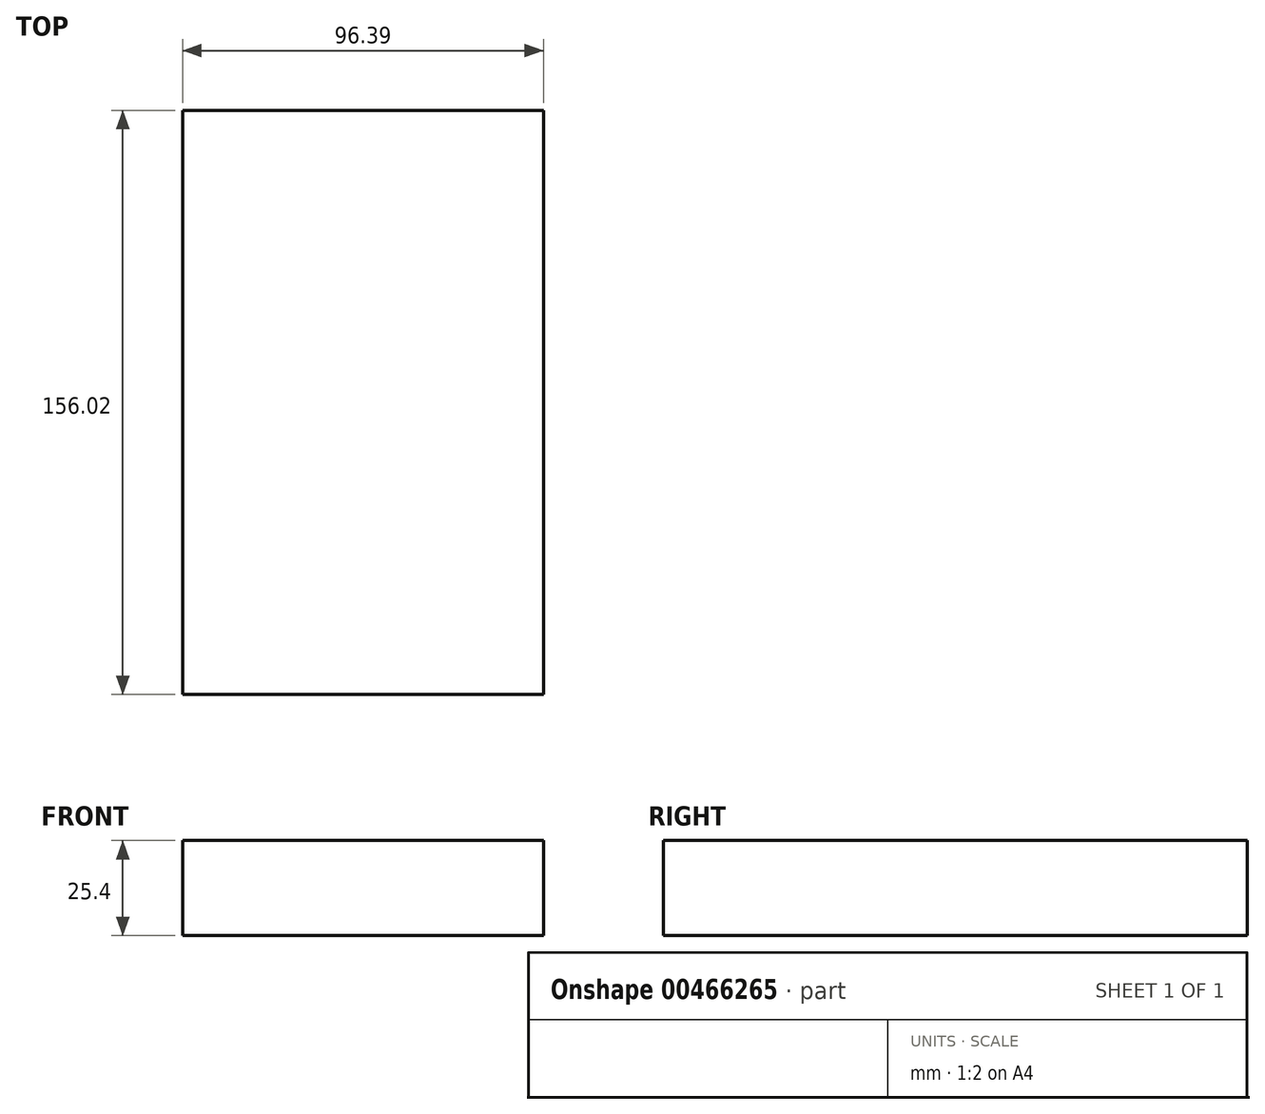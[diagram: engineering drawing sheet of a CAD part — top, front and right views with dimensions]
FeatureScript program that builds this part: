
annotation { "Feature Type Name" : "Feature", "Feature Type Description" : "" }
export const myFeature = defineFeature(function(context is Context, id is Id, definition is map)
    precondition{}
    {
        {
            var Q0;
            Q0=qCreatedBy(makeId("Top.planeOp"),FACE);
            var sketch = newSketch(context, id + "F0", { "sketchPlane" : qUnion([Q0])});
            skLineSegment(sketch, "E0.bottom", {"start": v(0, 96.14) * mm, "end": v(-96.39, 96.14) * mm});
            skLineSegment(sketch, "E0.top", {"start": v(0, -59.88) * mm, "end": v(-96.39, -59.88) * mm});
            skLineSegment(sketch, "E0.left", {"start": v(0, 96.14) * mm, "end": v(0, -59.88) * mm});
            skLineSegment(sketch, "E0.right", {"start": v(-96.39, 96.14) * mm, "end": v(-96.39, -59.88) * mm});
            skSolve(sketch);
        }
        {
            var Q0;
            Q0=makeQuery(id+"F0.imprint","IMPRINT",FACE,{"disambiguationData":[TD([[makeQuery(id+"F0.imprint","IMPRINT",EDGE,{"derivedFrom":sQuery(id+"F0.wireOp",EDGE,"E0.bottom")}),1.0]])]});
            extrude(context, id + "F1", {"entities" : qUnion([Q0]), "depth" : 25.4 * mm});
        }
    });
